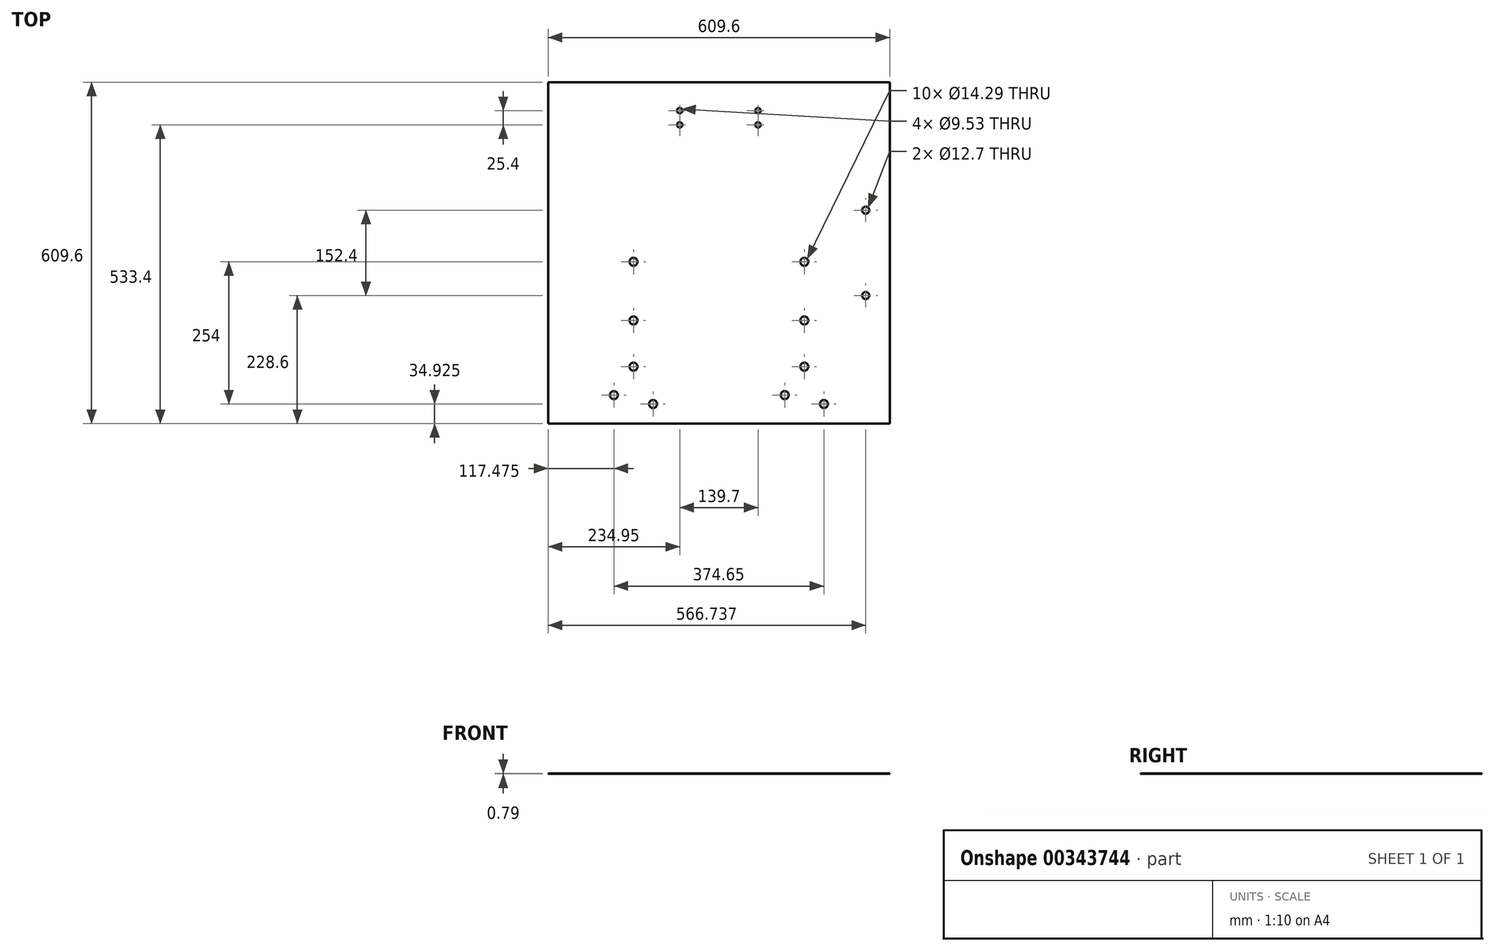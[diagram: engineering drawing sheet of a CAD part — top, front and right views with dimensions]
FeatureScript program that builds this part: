
annotation { "Feature Type Name" : "Feature", "Feature Type Description" : "" }
export const myFeature = defineFeature(function(context is Context, id is Id, definition is map)
    precondition{}
    {
        {
            var Q0;
            Q0=qCreatedBy(makeId("Top.planeOp"),FACE);
            var sketch = newSketch(context, id + "F0", { "sketchPlane" : qUnion([Q0])});
            skLineSegment(sketch, "E0.bottom", {"start": v(0, 0) * mm, "end": v(609.6, 0) * mm});
            skLineSegment(sketch, "E0.top", {"start": v(0, 609.6) * mm, "end": v(609.6, 609.6) * mm});
            skLineSegment(sketch, "E0.left", {"start": v(0, 0) * mm, "end": v(0, 609.6) * mm});
            skLineSegment(sketch, "E0.right", {"start": v(609.6, 0) * mm, "end": v(609.6, 609.6) * mm});
            skSolve(sketch);
        }
        {
            var Q0;
            Q0=makeQuery(id+"F0.imprint","IMPRINT",FACE,{"disambiguationData":[TD([[makeQuery(id+"F0.imprint","IMPRINT",EDGE,{"derivedFrom":sQuery(id+"F0.wireOp",EDGE,"E0.bottom")}),1.0]])]});
            extrude(context, id + "F1", {"entities" : qUnion([Q0]), "depth" : 0.8 * mm});
        }
        {
            var Q0;
            Q0=makeQuery(id+"F1.opExtrude","CAP_FACE",FACE,{"disambiguationData":[OSD([sQuery(id+"F0.wireOp",EDGE,"E0.bottom"),sQuery(id+"F0.wireOp",EDGE,"E0.top"),sQuery(id+"F0.wireOp",EDGE,"E0.left"),sQuery(id+"F0.wireOp",EDGE,"E0.right")])],"isStart":false});
            var sketch = newSketch(context, id + "F2", { "sketchPlane" : qUnion([Q0])});
            skLineSegment(sketch, "E1", {"start": v(152.4, 609.6) * mm, "end": v(152.4, 0) * mm, "construction": true});
            skLineSegment(sketch, "E2", {"start": v(304.8, 609.6) * mm, "end": v(304.8, 0) * mm, "construction": true});
            skPoint(sketch, "E2.endSnap0", {"position": v(304.8, 0) * mm});
            skCircle(sketch, "E3", {"center": v(152.4, 101.6) * mm, "radius": 7.14 * mm});
            skCircle(sketch, "E4", {"center": v(152.4, 184.15) * mm, "radius": 7.14 * mm});
            skCircle(sketch, "E5", {"center": v(152.4, 288.92) * mm, "radius": 7.14 * mm});
            skCircle(sketch, "E6", {"center": v(187.33, 34.92) * mm, "radius": 7.14 * mm});
            skCircle(sketch, "E7", {"center": v(117.48, 50.8) * mm, "radius": 7.14 * mm});
            skCircle(sketch, "E8.1.0.0", {"center": v(457.2, 288.93) * mm, "radius": 7.14 * mm});
            skCircle(sketch, "E8.1.0.1", {"center": v(457.2, 184.15) * mm, "radius": 7.14 * mm});
            skCircle(sketch, "E8.1.0.2", {"center": v(457.2, 101.6) * mm, "radius": 7.14 * mm});
            skCircle(sketch, "E8.1.0.3", {"center": v(422.28, 50.8) * mm, "radius": 7.14 * mm});
            skCircle(sketch, "E8.1.0.4", {"center": v(492.13, 34.93) * mm, "radius": 7.14 * mm});
            skLineSegment(sketch, "E8.direction1", {"start": v(152.4, 288.92) * mm, "end": v(457.2, 288.93) * mm, "construction": true});
            skSolve(sketch);
        }
        {
            var Q0;
            Q0=makeQuery(id+"F2.imprint","IMPRINT",FACE,{"disambiguationData":[TD([[makeQuery(id+"F2.imprint","IMPRINT",EDGE,{"derivedFrom":sQuery(id+"F2.wireOp",EDGE,"E6")}),1.0]])]});
            var Q1;
            Q1=makeQuery(id+"F2.imprint","IMPRINT",FACE,{"disambiguationData":[TD([[makeQuery(id+"F2.imprint","IMPRINT",EDGE,{"derivedFrom":sQuery(id+"F2.wireOp",EDGE,"E7")}),1.0]])]});
            var Q2;
            Q2=makeQuery(id+"F2.imprint","IMPRINT",FACE,{"disambiguationData":[TD([[makeQuery(id+"F2.imprint","IMPRINT",EDGE,{"derivedFrom":sQuery(id+"F2.wireOp",EDGE,"E3")}),1.0]])]});
            var Q3;
            Q3=makeQuery(id+"F2.imprint","IMPRINT",FACE,{"disambiguationData":[TD([[makeQuery(id+"F2.imprint","IMPRINT",EDGE,{"derivedFrom":sQuery(id+"F2.wireOp",EDGE,"E4")}),1.0]])]});
            var Q4;
            Q4=makeQuery(id+"F2.imprint","IMPRINT",FACE,{"disambiguationData":[TD([[makeQuery(id+"F2.imprint","IMPRINT",EDGE,{"derivedFrom":sQuery(id+"F2.wireOp",EDGE,"E5")}),1.0]])]});
            var Q5;
            Q5=makeQuery(id+"F2.imprint","IMPRINT",FACE,{"disambiguationData":[TD([[makeQuery(id+"F2.imprint","IMPRINT",EDGE,{"derivedFrom":sQuery(id+"F2.wireOp",EDGE,"3b4e70fb-c21b-4a0c-8268-0bb30d5104f20.MirrorC")}),-1.0]])]});
            var Q6;
            Q6=makeQuery(id+"F2.imprint","IMPRINT",FACE,{"disambiguationData":[TD([[makeQuery(id+"F2.imprint","IMPRINT",EDGE,{"derivedFrom":sQuery(id+"F2.wireOp",EDGE,"2f18fe3d-5e7c-4df9-aa36-324ae089a42a0.MirrorC")}),-1.0]])]});
            var Q7;
            Q7=makeQuery(id+"F2.imprint","IMPRINT",FACE,{"disambiguationData":[TD([[makeQuery(id+"F2.imprint","IMPRINT",EDGE,{"derivedFrom":sQuery(id+"F2.wireOp",EDGE,"3e35e3f6-8d9c-464a-875d-a1226e8cca760.MirrorC")}),-1.0]])]});
            var Q8;
            Q8=makeQuery(id+"F2.imprint","IMPRINT",FACE,{"disambiguationData":[TD([[makeQuery(id+"F2.imprint","IMPRINT",EDGE,{"derivedFrom":sQuery(id+"F2.wireOp",EDGE,"d1af4e2c-8dee-4732-b549-93060c32a8c20.MirrorC")}),-1.0]])]});
            var Q9;
            Q9=makeQuery(id+"F2.imprint","IMPRINT",FACE,{"disambiguationData":[TD([[makeQuery(id+"F2.imprint","IMPRINT",EDGE,{"derivedFrom":sQuery(id+"F2.wireOp",EDGE,"b2da134b-c416-4de1-a9ba-d3285da596360.MirrorC")}),-1.0]])]});
            var Q10;
            Q10=makeQuery(id+"F2.imprint","IMPRINT",FACE,{"disambiguationData":[TD([[makeQuery(id+"F2.imprint","IMPRINT",EDGE,{"derivedFrom":sQuery(id+"F2.wireOp",EDGE,"E8.1.0.0")}),1.0]])]});
            var Q11;
            Q11=makeQuery(id+"F2.imprint","IMPRINT",FACE,{"disambiguationData":[TD([[makeQuery(id+"F2.imprint","IMPRINT",EDGE,{"derivedFrom":sQuery(id+"F2.wireOp",EDGE,"E8.1.0.1")}),1.0]])]});
            var Q12;
            Q12=makeQuery(id+"F2.imprint","IMPRINT",FACE,{"disambiguationData":[TD([[makeQuery(id+"F2.imprint","IMPRINT",EDGE,{"derivedFrom":sQuery(id+"F2.wireOp",EDGE,"E8.1.0.2")}),1.0]])]});
            var Q13;
            Q13=makeQuery(id+"F2.imprint","IMPRINT",FACE,{"disambiguationData":[TD([[makeQuery(id+"F2.imprint","IMPRINT",EDGE,{"derivedFrom":sQuery(id+"F2.wireOp",EDGE,"E8.1.0.3")}),1.0]])]});
            var Q14;
            Q14=makeQuery(id+"F2.imprint","IMPRINT",FACE,{"disambiguationData":[TD([[makeQuery(id+"F2.imprint","IMPRINT",EDGE,{"derivedFrom":sQuery(id+"F2.wireOp",EDGE,"E8.1.0.4")}),1.0]])]});
            extrude(context, id + "F3", {"entities" : qUnion([Q0, Q1, Q2, Q3, Q4, Q5, Q6, Q7, Q8, Q9, Q10, Q11, Q12, Q13, Q14]), "operationType" : NewBodyOperationType.REMOVE, "oppositeDirection" : true, "depth" : 25.4 * mm});
        }
        {
            var Q0;
            Q0=makeQuery(id+"F1.opExtrude","CAP_FACE",FACE,{"disambiguationData":[OSD([sQuery(id+"F0.wireOp",EDGE,"E0.bottom"),sQuery(id+"F0.wireOp",EDGE,"E0.top"),sQuery(id+"F0.wireOp",EDGE,"E0.left"),sQuery(id+"F0.wireOp",EDGE,"E0.right")])],"isStart":false});
            var sketch = newSketch(context, id + "F4", { "sketchPlane" : qUnion([Q0])});
            skCircle(sketch, "E9", {"center": v(234.95, 558.8) * mm, "radius": 4.76 * mm});
            skCircle(sketch, "E10", {"center": v(234.95, 533.4) * mm, "radius": 4.76 * mm});
            skCircle(sketch, "E11", {"center": v(374.65, 558.8) * mm, "radius": 4.76 * mm});
            skCircle(sketch, "E12", {"center": v(374.65, 533.4) * mm, "radius": 4.76 * mm});
            skSolve(sketch);
        }
        {
            var Q0;
            Q0=makeQuery(id+"F4.imprint","IMPRINT",FACE,{"disambiguationData":[TD([[makeQuery(id+"F4.imprint","IMPRINT",EDGE,{"derivedFrom":sQuery(id+"F4.wireOp",EDGE,"E9")}),1.0]])]});
            var Q1;
            Q1=makeQuery(id+"F4.imprint","IMPRINT",FACE,{"disambiguationData":[TD([[makeQuery(id+"F4.imprint","IMPRINT",EDGE,{"derivedFrom":sQuery(id+"F4.wireOp",EDGE,"E10")}),1.0]])]});
            var Q2;
            Q2=makeQuery(id+"F4.imprint","IMPRINT",FACE,{"disambiguationData":[TD([[makeQuery(id+"F4.imprint","IMPRINT",EDGE,{"derivedFrom":sQuery(id+"F4.wireOp",EDGE,"E12")}),1.0]])]});
            var Q3;
            Q3=makeQuery(id+"F4.imprint","IMPRINT",FACE,{"disambiguationData":[TD([[makeQuery(id+"F4.imprint","IMPRINT",EDGE,{"derivedFrom":sQuery(id+"F4.wireOp",EDGE,"E11")}),1.0]])]});
            extrude(context, id + "F5", {"entities" : qUnion([Q0, Q1, Q2, Q3]), "operationType" : NewBodyOperationType.REMOVE, "oppositeDirection" : true, "depth" : 25.4 * mm});
        }
        {
            var Q0;
            Q0=makeQuery(id+"F1.opExtrude","CAP_FACE",FACE,{"disambiguationData":[OSD([sQuery(id+"F0.wireOp",EDGE,"E0.bottom"),sQuery(id+"F0.wireOp",EDGE,"E0.top"),sQuery(id+"F0.wireOp",EDGE,"E0.left"),sQuery(id+"F0.wireOp",EDGE,"E0.right")])],"isStart":true});
            var sketch = newSketch(context, id + "F6", { "sketchPlane" : qUnion([Q0])});
            skLineSegment(sketch, "E13", {"start": v(609.6, -152.4) * mm, "end": v(0, -152.4) * mm, "construction": true});
            skLineSegment(sketch, "E14", {"start": v(609.6, -457.2) * mm, "end": v(0, -457.2) * mm, "construction": true});
            skLineSegment(sketch, "E15", {"start": v(587.38, -609.6) * mm, "end": v(587.38, 0) * mm, "construction": true});
            skCircle(sketch, "E16", {"center": v(566.74, -228.6) * mm, "radius": 6.35 * mm});
            skCircle(sketch, "E17", {"center": v(566.74, -381) * mm, "radius": 6.35 * mm});
            skSolve(sketch);
        }
        {
            var Q0;
            Q0=makeQuery(id+"F6.imprint","IMPRINT",FACE,{"disambiguationData":[TD([[makeQuery(id+"F6.imprint","IMPRINT",EDGE,{"derivedFrom":sQuery(id+"F6.wireOp",EDGE,"E17")}),1.0]])]});
            var Q1;
            Q1=makeQuery(id+"F6.imprint","IMPRINT",FACE,{"disambiguationData":[TD([[makeQuery(id+"F6.imprint","IMPRINT",EDGE,{"derivedFrom":sQuery(id+"F6.wireOp",EDGE,"E16")}),1.0]])]});
            extrude(context, id + "F7", {"entities" : qUnion([Q0, Q1]), "operationType" : NewBodyOperationType.REMOVE, "oppositeDirection" : true, "depth" : 25.4 * mm});
        }
    });
